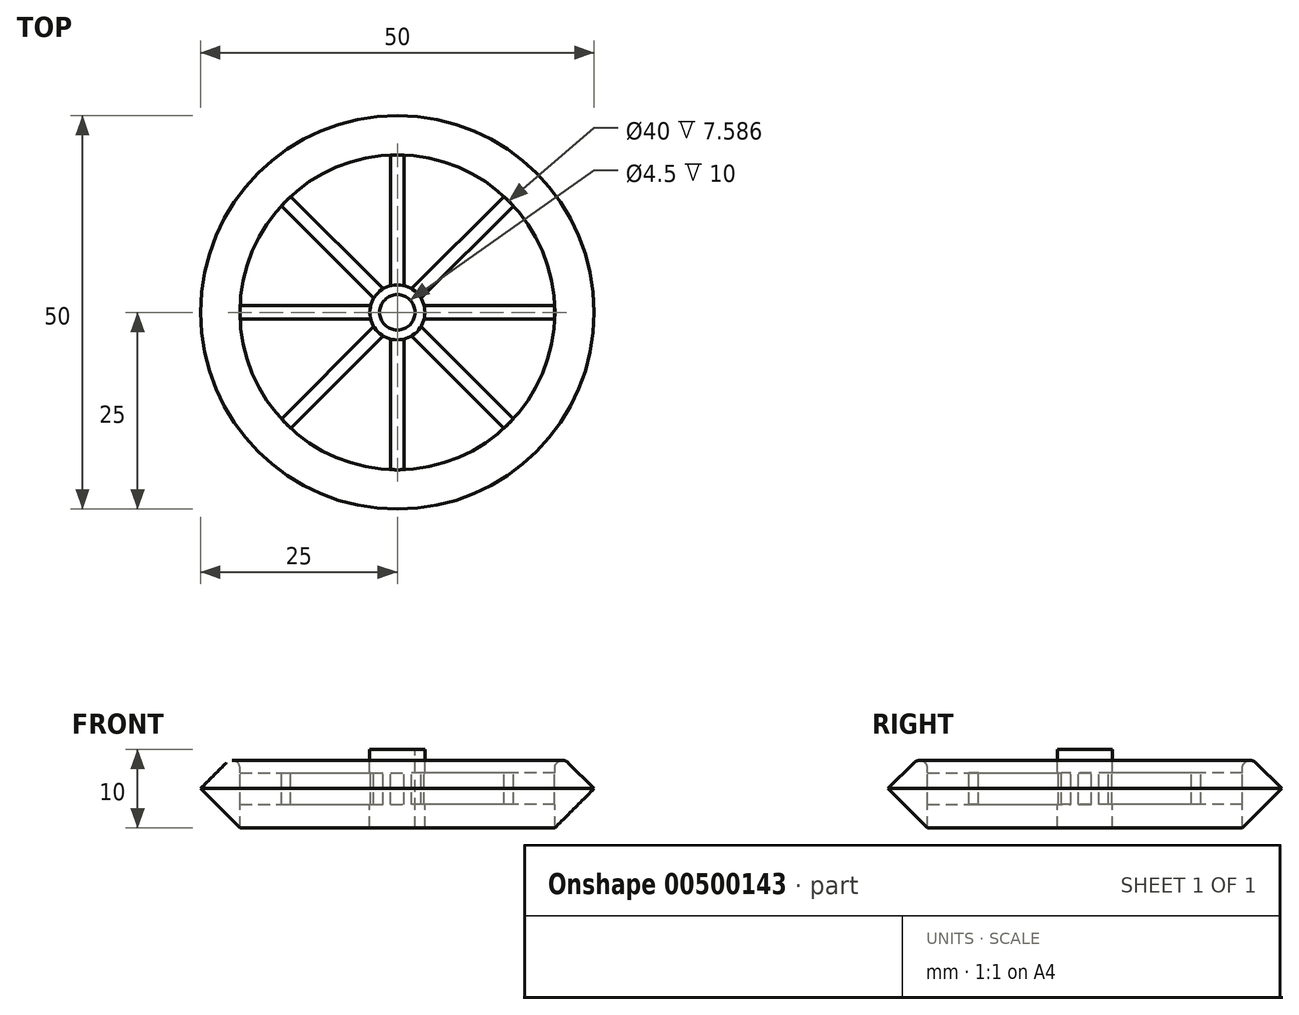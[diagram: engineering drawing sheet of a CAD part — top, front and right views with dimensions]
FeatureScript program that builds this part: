
annotation { "Feature Type Name" : "Feature", "Feature Type Description" : "" }
export const myFeature = defineFeature(function(context is Context, id is Id, definition is map)
    precondition{}
    {
        {
            var Q0;
            Q0=qCreatedBy(makeId("Top.planeOp"),FACE);
            var sketch = newSketch(context, id + "F0", { "sketchPlane" : qUnion([Q0])});
            skCircle(sketch, "E0", {"center": v(0, 0) * mm, "radius": 25 * mm});
            skSolve(sketch);
        }
        {
            var Q0;
            Q0=makeQuery(id+"F0.imprint","IMPRINT",FACE,{"disambiguationData":[TD([[makeQuery(id+"F0.imprint","IMPRINT",EDGE,{"derivedFrom":sQuery(id+"F0.wireOp",EDGE,"E0")}),1.0]])]});
            extrude(context, id + "F1", {"entities" : qUnion([Q0]), "endBound" : BoundingType.SYMMETRIC, "depth" : 10 * mm});
        }
        {
            var Q0;
            Q0=makeQuery(id+"F1.opExtrude","SWEPT_FACE",FACE,{"disambiguationData":[OSD([sQuery(id+"F0.wireOp",EDGE,"E0")])]});
            chamfer(context, id + "F2", {"entities" : qUnion([Q0]), "width" : 5 * mm, "tangentPropagation" : true});
        }
        {
            var Q0;
            Q0=makeQuery(id+"F1.opExtrude","CAP_FACE",FACE,{"disambiguationData":[OSD([sQuery(id+"F0.wireOp",EDGE,"E0")])],"isStart":false});
            var sketch = newSketch(context, id + "F3", { "sketchPlane" : qUnion([Q0])});
            skCircle(sketch, "E1", {"center": v(0, 0) * mm, "radius": 3.5 * mm});
            skCircle(sketch, "E2", {"center": v(0, 0) * mm, "radius": 2.25 * mm});
            skSolve(sketch);
        }
        {
            var Q0;
            Q0=makeQuery(id+"F3.imprint","IMPRINT",FACE,{"disambiguationData":[TD([[makeQuery(id+"F3.imprint","IMPRINT",EDGE,{"derivedFrom":sQuery(id+"F3.wireOp",EDGE,"E1")}),-1.0]])]});
            extrude(context, id + "F4", {"entities" : qUnion([Q0]), "operationType" : NewBodyOperationType.REMOVE, "oppositeDirection" : true, "depth" : 25 * mm, "offsetDistance" : 25 * mm});
        }
        {
            var Q0;
            Q0=makeQuery(id+"F3.imprint","IMPRINT",FACE,{"disambiguationData":[TD([[makeQuery(id+"F3.imprint","IMPRINT",EDGE,{"derivedFrom":sQuery(id+"F3.wireOp",EDGE,"E2")}),1.0]])]});
            extrude(context, id + "F5", {"entities" : qUnion([Q0]), "operationType" : NewBodyOperationType.REMOVE, "endBound" : BoundingType.SYMMETRIC, "oppositeDirection" : true, "depth" : 25 * mm, "offsetDistance" : 25 * mm});
        }
        {
            var Q0;
            Q0=qCreatedBy(makeId("Top.planeOp"),FACE);
            var sketch = newSketch(context, id + "F6", { "sketchPlane" : qUnion([Q0])});
            skPoint(sketch, "E3.1.internal.snap0", {"position": v(0, -8.07) * mm});
            skLineSegment(sketch, "E4", {"start": v(0, -3.12) * mm, "end": v(0, -21.52) * mm});
            skLineSegment(sketch, "E5", {"start": v(0, -21.52) * mm, "end": v(-0.84, -21.52) * mm});
            skLineSegment(sketch, "E6", {"start": v(-0.84, -21.52) * mm, "end": v(-0.84, -2.91) * mm});
            skLineSegment(sketch, "E7", {"start": v(-0.84, -2.91) * mm, "end": v(0, -3.12) * mm});
            skLineSegment(sketch, "E8.MirrorCS", {"start": v(0.84, -2.91) * mm, "end": v(0, -3.12) * mm});
            skLineSegment(sketch, "E9.MirrorCS", {"start": v(0.84, -21.52) * mm, "end": v(0.84, -2.91) * mm});
            skLineSegment(sketch, "E10.MirrorCS", {"start": v(0, -21.52) * mm, "end": v(0.84, -21.52) * mm});
            skSolve(sketch);
        }
        {
            var Q0;
            Q0 = qSketchRegion(id + "F6", true);
            extrude(context, id + "F7", {"entities" : qUnion([Q0]), "endBound" : BoundingType.SYMMETRIC, "depth" : 4 * mm, "offsetDistance" : 25 * mm});
        }
        {
            var Q0;
            Q0=qCreatedBy(makeId("Front.planeOp"),FACE);
            var sketch = newSketch(context, id + "F8", { "sketchPlane" : qUnion([Q0])});
            skLineSegment(sketch, "E11", {"start": v(0, 10.65) * mm, "end": v(0, -10.07) * mm});
            skSolve(sketch);
        }
        {
            var Q0;
            Q0=makeQuery(id+"F7.opExtrude","SWEPT_BODY",BODY,{"disambiguationData":[OSD([sQuery(id+"F6.wireOp",EDGE,"E5"),sQuery(id+"F6.wireOp",EDGE,"E6"),sQuery(id+"F6.wireOp",EDGE,"E7"),sQuery(id+"F6.wireOp",EDGE,"E8.MirrorCS"),sQuery(id+"F6.wireOp",EDGE,"E9.MirrorCS"),sQuery(id+"F6.wireOp",EDGE,"E10.MirrorCS")])]});
            var Q1;
            Q1=sQuery(id+"F8.wireOp",EDGE,"E11");
            circularPattern(context, id + "F9", {"operationType" : NewBodyOperationType.ADD, "entities" : qUnion([Q0]), "axis" : qUnion([Q1]), "angle" : 360 * degree, "instanceCount" : 8, "equalSpace" : true});
        }
        {
            var Q0;
            {var subQ0=sQuery(id+"F0.wireOp",EDGE,"E0");Q0=makeQuery(id+"F4.boolean.opBoolean","MERGE",EDGE,{"derivedFrom":[makeQuery(id+"F2.opChamfer","BLEND_EDGE",EDGE,{"blendedFrom":[makeQuery(id+"F1.opExtrude","CAP_EDGE",EDGE,{"disambiguationData":[OSD([subQ0])],"isStart":false}),makeQuery(id+"F1.opExtrude","CAP_FACE",FACE,{"disambiguationData":[OSD([subQ0])],"isStart":false})],"blendedInto":[makeQuery(id+"F1.opExtrude","CAP_FACE",FACE,{"disambiguationData":[OSD([subQ0])],"isStart":false})]}),makeQuery(id+"F4.opExtrude","CAP_EDGE",EDGE,{"disambiguationData":[OSD([subQ0])],"isStart":true})]});}
            var Q1;
            {var subQ0=sQuery(id+"F0.wireOp",EDGE,"E0");Q1=makeQuery(id+"F2.opChamfer","BLEND_EDGE",EDGE,{"blendedFrom":[makeQuery(id+"F1.opExtrude","CAP_EDGE",EDGE,{"disambiguationData":[OSD([subQ0])],"isStart":true}),makeQuery(id+"F1.opExtrude","CAP_FACE",FACE,{"disambiguationData":[OSD([subQ0])],"isStart":true})],"blendedInto":[makeQuery(id+"F1.opExtrude","CAP_FACE",FACE,{"disambiguationData":[OSD([subQ0])],"isStart":true})]});}
            fillet(context, id + "F10", {"entities" : qUnion([Q0, Q1]), "radius" : 1 * mm, "tangentPropagation" : true, "allowEdgeOverflow" : false});
        }
    });
